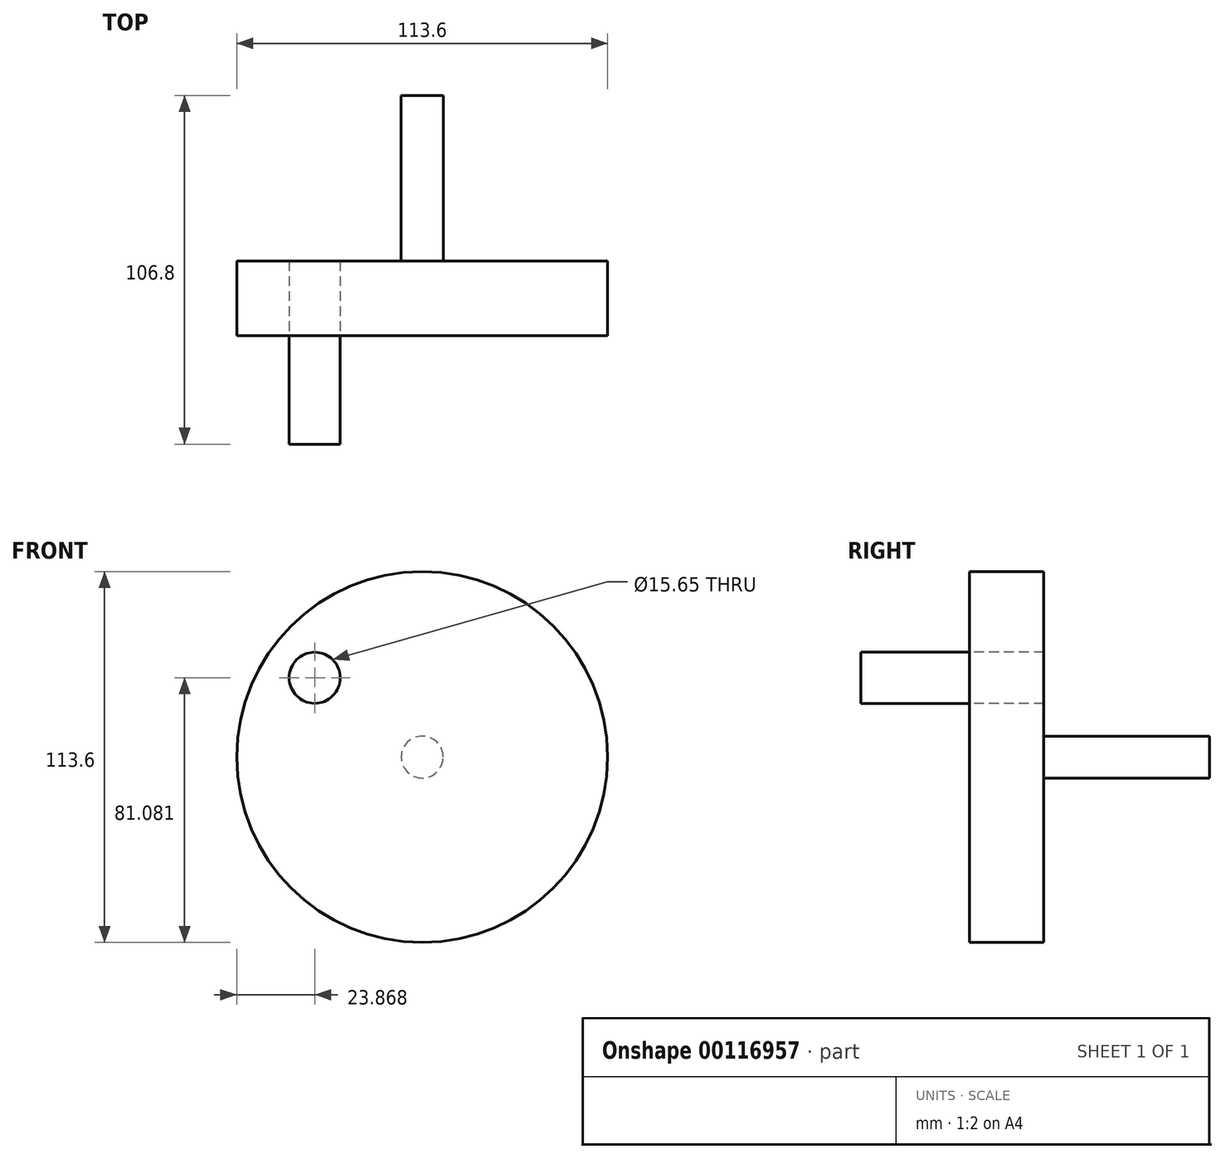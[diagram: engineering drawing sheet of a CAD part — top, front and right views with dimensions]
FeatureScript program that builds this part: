
annotation { "Feature Type Name" : "Feature", "Feature Type Description" : "" }
export const myFeature = defineFeature(function(context is Context, id is Id, definition is map)
    precondition{}
    {
        {
            var Q0;
            Q0=qCreatedBy(makeId("Front.planeOp"),FACE);
            var sketch = newSketch(context, id + "F0", { "sketchPlane" : qUnion([Q0])});
            skCircle(sketch, "E0", {"center": v(0, 0) * mm, "radius": 56.8 * mm});
            skCircle(sketch, "E1", {"center": v(-32.93, 24.28) * mm, "radius": 7.82 * mm});
            skSolve(sketch);
        }
        {
            var Q0;
            Q0=makeQuery(id+"F0.imprint","IMPRINT",FACE,{"disambiguationData":[TD([[makeQuery(id+"F0.imprint","IMPRINT",EDGE,{"derivedFrom":sQuery(id+"F0.wireOp",EDGE,"E1")}),1.0]])]});
            extrude(context, id + "F1", {"entities" : qUnion([Q0]), "depth" : 33.24 * mm});
        }
        {
            var Q0;
            Q0=makeQuery(id+"F0.imprint","IMPRINT",FACE,{"disambiguationData":[TD([[makeQuery(id+"F0.imprint","IMPRINT",EDGE,{"derivedFrom":sQuery(id+"F0.wireOp",EDGE,"E0")}),1.0]])]});
            extrude(context, id + "F2", {"entities" : qUnion([Q0]), "oppositeDirection" : true, "depth" : 22.83 * mm});
        }
        {
            var Q0;
            Q0=sQuery(id+"F0.wireOp",VERTEX,"E0.center");
            var Q1;
            Q1=makeQuery(id+"F2.opExtrude","SWEPT_BODY",BODY,{"disambiguationData":[OSD([sQuery(id+"F0.wireOp",EDGE,"E0"),sQuery(id+"F0.wireOp",EDGE,"E1")])]});
            hole(context, id + "F3", {"style" : HoleStyle.SIMPLE, "endStyle" : HoleEndStyle.THROUGH, "holeDiameter" : 12.75 * mm, "locations" : qUnion([Q0]), "scope" : qUnion([Q1]), "isTappedThrough" : true});
        }
        {
            var Q0;
            Q0=makeQuery(id+"F0.imprint","IMPRINT",FACE,{"disambiguationData":[TD([[makeQuery(id+"F0.imprint","IMPRINT",EDGE,{"derivedFrom":sQuery(id+"F0.wireOp",EDGE,"E1")}),1.0]])]});
            extrude(context, id + "F4", {"entities" : qUnion([Q0]), "oppositeDirection" : true, "depth" : 22.8 * mm});
        }
        {
            var Q0;
            Q0=qCreatedBy(makeId("Front.planeOp"),FACE);
            var sketch = newSketch(context, id + "F5", { "sketchPlane" : qUnion([Q0])});
            skCircle(sketch, "E2", {"center": v(0, 0) * mm, "radius": 6.42 * mm});
            skSolve(sketch);
        }
        {
            var Q0;
            Q0 = qSketchRegion(id + "F5", true);
            extrude(context, id + "F6", {"entities" : qUnion([Q0]), "operationType" : NewBodyOperationType.ADD, "oppositeDirection" : true, "depth" : 73.56 * mm});
        }
    });
